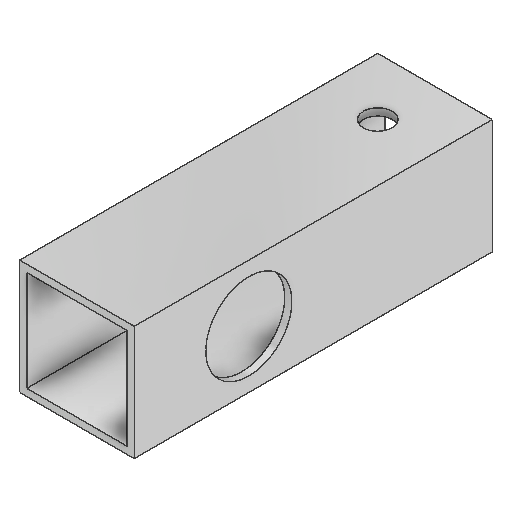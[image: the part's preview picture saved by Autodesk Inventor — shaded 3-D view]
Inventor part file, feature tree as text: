
AUTODESK INVENTOR PART (.ipt)
format: ipt  version: 2025.2 (Build 292293000, 293)  size: 142,336 bytes
history: native  units: in
note: dims shown in document units (in); Inventor stores cm internally (conversion verified against a paired STEP export)
features: extrude x3, sketch x3
ambient origin geometry x8: Origin, YZ Plane, XZ Plane, XY Plane, X Axis, Y Axis, Z Axis, Center Point
bodies: Solid1 (feature_tree)
feature tree (6):
  extrude  "Extrusion1"  Depth=1.0in
  extrude  "Extrusion2"  Depth=0.0625in
  extrude  "Extrusion3"  Depth=0.0625in
  sketch  "Sketch1"  dims[d0=1.0in d1=1.0in]
  sketch  "Sketch2"  dims[d2=0.0625in d3=0.0625in]
  sketch  "Sketch3"  dims[d4=0.0625in d5=0.0625in d6=3.125in d7=0.0in d8=0.75in d9=0.0in d10=0.0in d11=0.5in d12=1.0in d13=0.8in d14=0.25in d15=0.25in d16=0.8in d17=0.25in d18=0.5in d19=0.5in d20=0.0in d21=0.0in]
